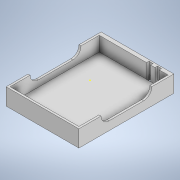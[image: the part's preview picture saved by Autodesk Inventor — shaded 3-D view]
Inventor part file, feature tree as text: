
AUTODESK INVENTOR PART (.ipt)
format: ipt  version: 2021.2 (Build 252289000, 289)  size: 210,432 bytes
history: native  units: in
note: dims shown in document units (in); Inventor stores cm internally (conversion verified against a paired STEP export)
features: sketch x8, extrude x7, fillet x1
ambient origin geometry x8: Origin, YZ Plane, XZ Plane, XY Plane, X Axis, Y Axis, Z Axis, Center Point
bodies: Solid1 (feature_tree)
feature tree (16):
  extrude  "Extrusion1"  Depth=1.8386in
  extrude  "Extrusion2"  Depth=0.7047in
  extrude  "Extrusion6"  Depth=0.0433in
  fillet  "Fillet2"  Radius=0.0433in
  sketch  "Sketch9"  dims[d8=0.0433in d9=0.0787in]
  extrude  "Extrusion9"  Depth=0.0787in
  extrude  "Extrusion11"  Depth=0.2795in
  extrude  "Extrusion12"  Depth=0.1575in
  extrude  "Extrusion13"  Depth=0.1575in
  sketch  "Sketch1"  dims[d0=1.4094in d1=1.8386in]
  sketch  "Sketch2"  dims[d2=0.9193in d3=0.7047in]
  sketch  "Sketch6"  dims[d4=0.3228in d5=0.0in d6=0.0433in d7=0.0433in]
  sketch  "Sketch10"  dims[d10=0.2795in d11=0.0in d34=0.9843in]
  sketch  "Sketch12"  dims[d35=0.4272in d36=0.1575in]
  sketch  "Sketch13"  dims[d37=0.0in d38=0.0in d39=0.1575in]
  sketch  "Sketch14"  dims[d51=0.0787in d52=0.0787in d53=0.0868in d54=0.0394in d55=0.2106in d56=0.0in d57=0.0in d64=0.0in d65=0.0in d66=0.0984in d67=0.3937in d68=0.0in d69=0.0039in d70=0.0039in d71=0.0039in d72=0.0039in d73=0.3937in d74=0.0in d20=0.0197in d21=0.0344in d22=0.0197in d23=0.0344in d25=0.0197in d26=0.0344in d27=0.0197in d28=0.0344in]
